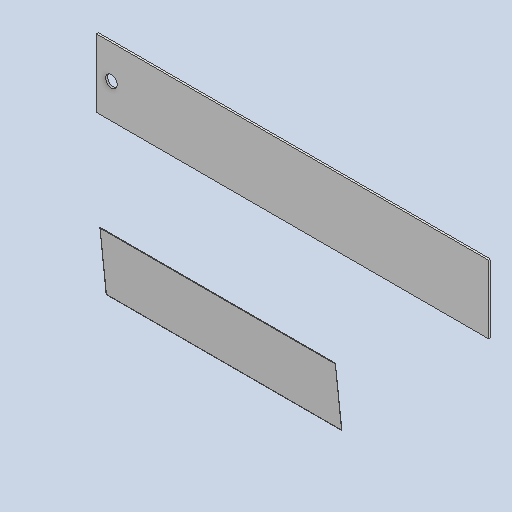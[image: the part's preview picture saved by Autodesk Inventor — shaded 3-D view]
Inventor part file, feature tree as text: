
AUTODESK INVENTOR PART (.ipt)
format: ipt  version: 2023 (Build 270158000, 158)  size: 149,504 bytes
history: native  units: in
note: dims shown in document units (in); Inventor stores cm internally (conversion verified against a paired STEP export)
features: other x9, reference x7, extrude x5, sketch x5, projected_geometry x3
ambient origin geometry x8: Origin, YZ Plane, XZ Plane, XY Plane, X Axis, Y Axis, Z Axis, Center Point
bodies: Body1 (feature_tree)
feature tree (29):
  other  "Bryła1"
  extrude  "Wyciągnięcie proste1"  Depth=0.1181in
  sketch  "Szkic2"
  other  "Płaszczyzna konstrukcyjna1"
  extrude  "Wyciągnięcie proste2"  Depth=2.3622in
  extrude  "Wyciągnięcie proste3"  Depth=0.7874in
  extrude  "Wyciągnięcie proste4"  Depth=0.0197in TaperAngle=0.0deg
  extrude  "Wyciągnięcie proste5"  Depth=0.0197in TaperAngle=0.0deg
  sketch  "Szkic1"
  reference  "Odniesienie1"
  reference  "Odniesienie2"
  reference  "Odniesienie3"
  projected_geometry  "Pętla rzutowana1"
  sketch  "Szkic3"
  projected_geometry  "Pętla rzutowana2"
  reference  "Odniesienie4"
  reference  "Odniesienie5"
  sketch  "Szkic4"
  projected_geometry  "Pętla rzutowana3"
  sketch  "Szkic5"
  reference  "Odniesienie6"
  reference  "Odniesienie7"
  other  "<userpath>\Desktop\MojeRoboty\Stefan\mechanics 2\STEFAN.iam"
  other  "STEFAN.iam"
  other  "sciana_prawa_nowa_MIR:1"
  other  "sciana_prawa_nowa:1"
  other  "dach:1"
  other  "uchwyt_silnikow:1"
  other  "podstawa:1"
